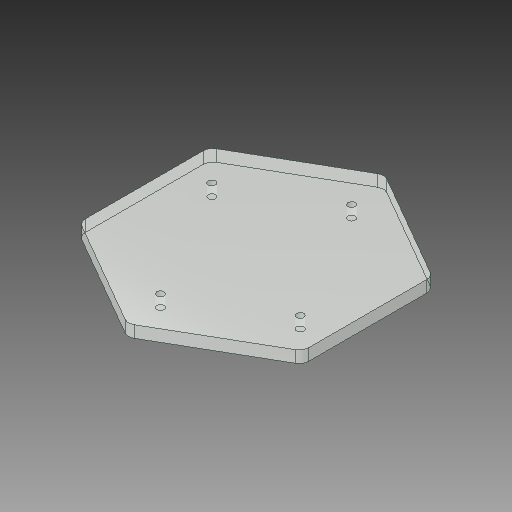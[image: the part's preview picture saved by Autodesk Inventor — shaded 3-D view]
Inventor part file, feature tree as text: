
AUTODESK INVENTOR PART (.ipt)
format: ipt  version: 2018 (Build 220112000, 112)  size: 150,528 bytes
history: native  units: mm
features: sketch x1, extrude x1, fillet x1
ambient origin geometry x8: Origin, YZ Plane, XZ Plane, XY Plane, X Axis, Y Axis, Z Axis, Center Point
bodies: Body1 (feature_tree)
feature tree (3):
  sketch  "Sketch1"  dims[d0=54.864mm d1=0.0mm d3=39.0mm d4=4.5mm d5=4.5mm d6=4.5mm d7=4.5mm d9=4.5mm d11=4.5mm d15=4.5mm d21=5.0mm d22=0.0mm d28=4.0mm]
  extrude  "Extrusion2"  Depth=5.0mm TaperAngle=0.0deg
  fillet  "Fillet1"  Radius=4.0mm
